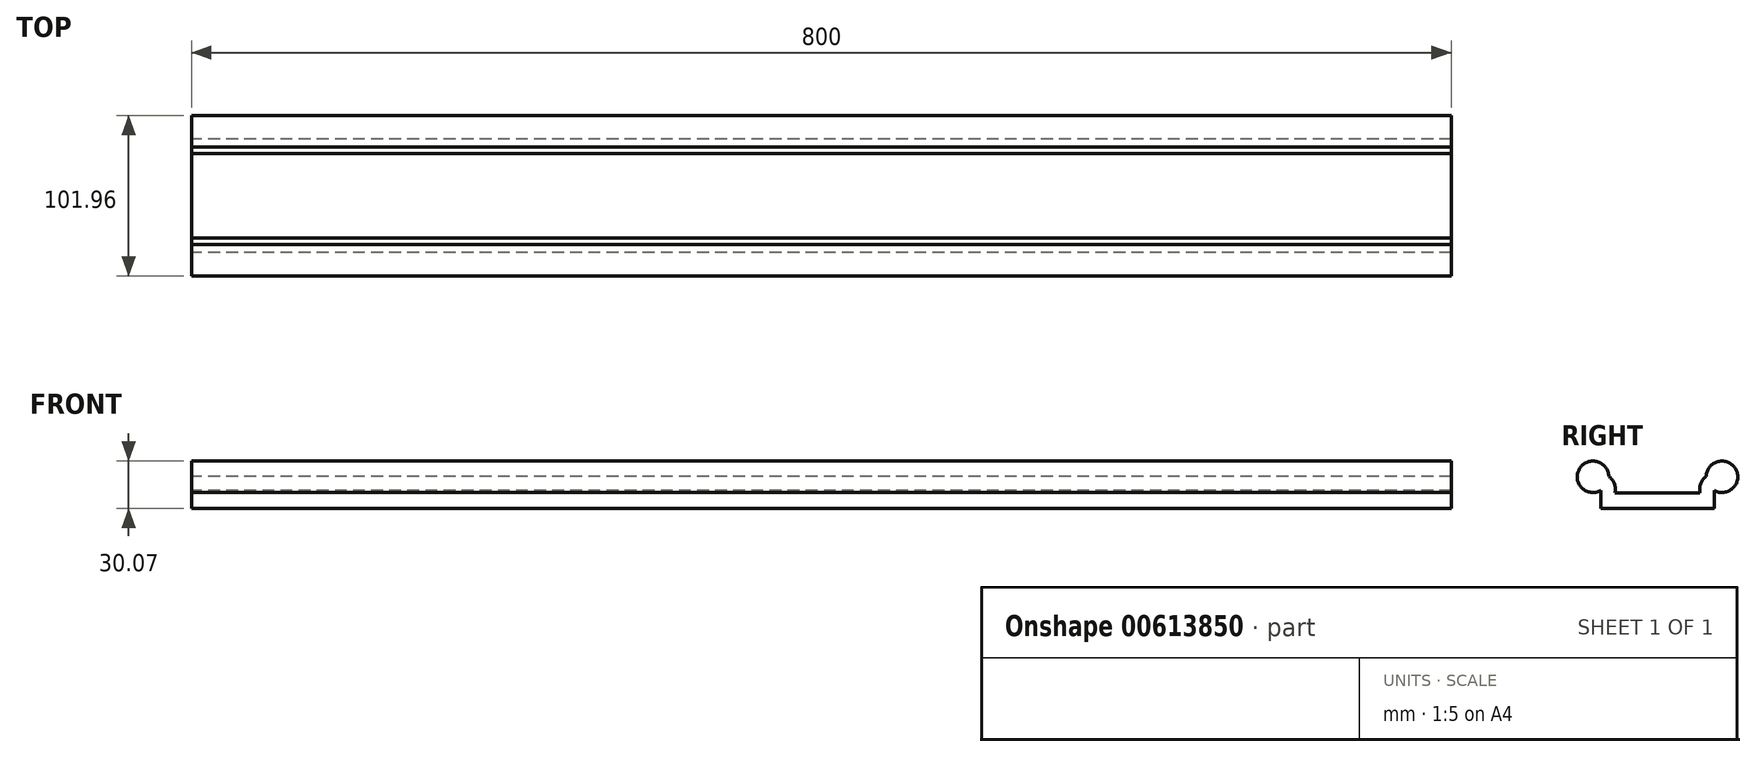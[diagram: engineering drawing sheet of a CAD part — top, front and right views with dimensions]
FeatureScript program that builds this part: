
annotation { "Feature Type Name" : "Feature", "Feature Type Description" : "" }
export const myFeature = defineFeature(function(context is Context, id is Id, definition is map)
    precondition{}
    {
        {
            var Q0;
            Q0=qCreatedBy(makeId("Right.planeOp"),FACE);
            var sketch = newSketch(context, id + "F0", { "sketchPlane" : qUnion([Q0])});
            skCircle(sketch, "E0", {"center": v(40.98, 20.07) * mm, "radius": 10 * mm});
            skLineSegment(sketch, "E1", {"start": v(36, 0) * mm, "end": v(36, 11.4) * mm});
            skPoint(sketch, "E2", {"position": v(0, 9.9) * mm});
            skArc(sketch, "E3", {"start": v(30.98, 20.35) * mm, "mid": v(27.45, 15.72) * mm, "end": v(26.98, 9.9) * mm});
            skLineSegment(sketch, "E4", {"start": v(0, 9.9) * mm, "end": v(26.98, 9.9) * mm});
            skLineSegment(sketch, "E5", {"start": v(0, 9.9) * mm, "end": v(0, 0) * mm});
            skLineSegment(sketch, "E6", {"start": v(0, 0) * mm, "end": v(36, 0) * mm});
            skLineSegment(sketch, "E7.MirrorCS", {"start": v(0, 9.9) * mm, "end": v(-26.98, 9.9) * mm});
            skArc(sketch, "E8.MirrorCS", {"start": v(-30.98, 20.35) * mm, "mid": v(-27.45, 15.72) * mm, "end": v(-26.98, 9.9) * mm});
            skCircle(sketch, "E9.MirrorC", {"center": v(-40.98, 20.07) * mm, "radius": 10 * mm});
            skLineSegment(sketch, "E10.MirrorCS", {"start": v(-36, 0) * mm, "end": v(-36, 11.4) * mm});
            skLineSegment(sketch, "E11.MirrorCS", {"start": v(0, 0) * mm, "end": v(-36, 0) * mm});
            skSolve(sketch);
        }
        {
            var Q0;
            Q0 = qSketchRegion(id + "F0", true);
            extrude(context, id + "F1", {"entities" : qUnion([Q0]), "endBound" : BoundingType.SYMMETRIC, "depth" : 800 * mm, "offsetDistance" : 25.4 * mm});
        }
    });
